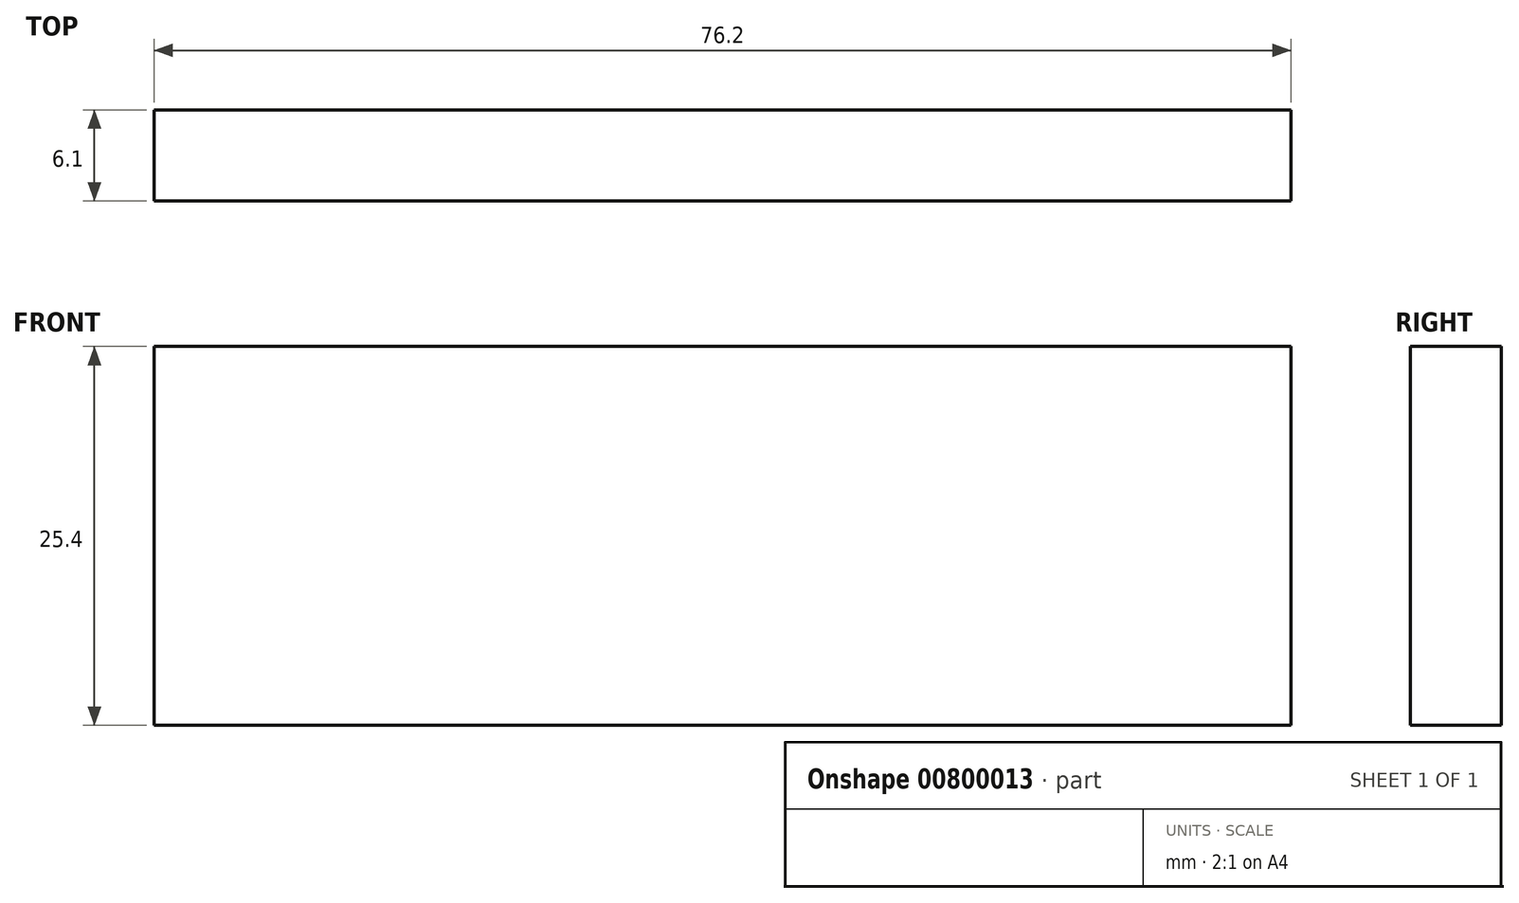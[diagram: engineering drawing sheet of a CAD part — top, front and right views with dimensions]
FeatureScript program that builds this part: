
annotation { "Feature Type Name" : "Feature", "Feature Type Description" : "" }
export const myFeature = defineFeature(function(context is Context, id is Id, definition is map)
    precondition{}
    {
        {
            var Q0;
            Q0=qCreatedBy(makeId("Front.planeOp"),FACE);
            var sketch = newSketch(context, id + "F0", { "sketchPlane" : qUnion([Q0])});
            skLineSegment(sketch, "E0", {"start": v(-37.68, 11.81) * mm, "end": v(38.52, 11.81) * mm});
            skLineSegment(sketch, "E1", {"start": v(38.52, 11.81) * mm, "end": v(38.52, -13.59) * mm});
            skLineSegment(sketch, "E2", {"start": v(38.52, -13.59) * mm, "end": v(-37.68, -13.59) * mm});
            skLineSegment(sketch, "E3", {"start": v(-37.68, -13.59) * mm, "end": v(-37.68, 11.81) * mm});
            skSolve(sketch);
        }
        {
            var Q0;
            Q0 = qSketchRegion(id + "F0", true);
            extrude(context, id + "F1", {"entities" : qUnion([Q0]), "depth" : 6.1 * mm, "offsetDistance" : 25.4 * mm});
        }
    });
